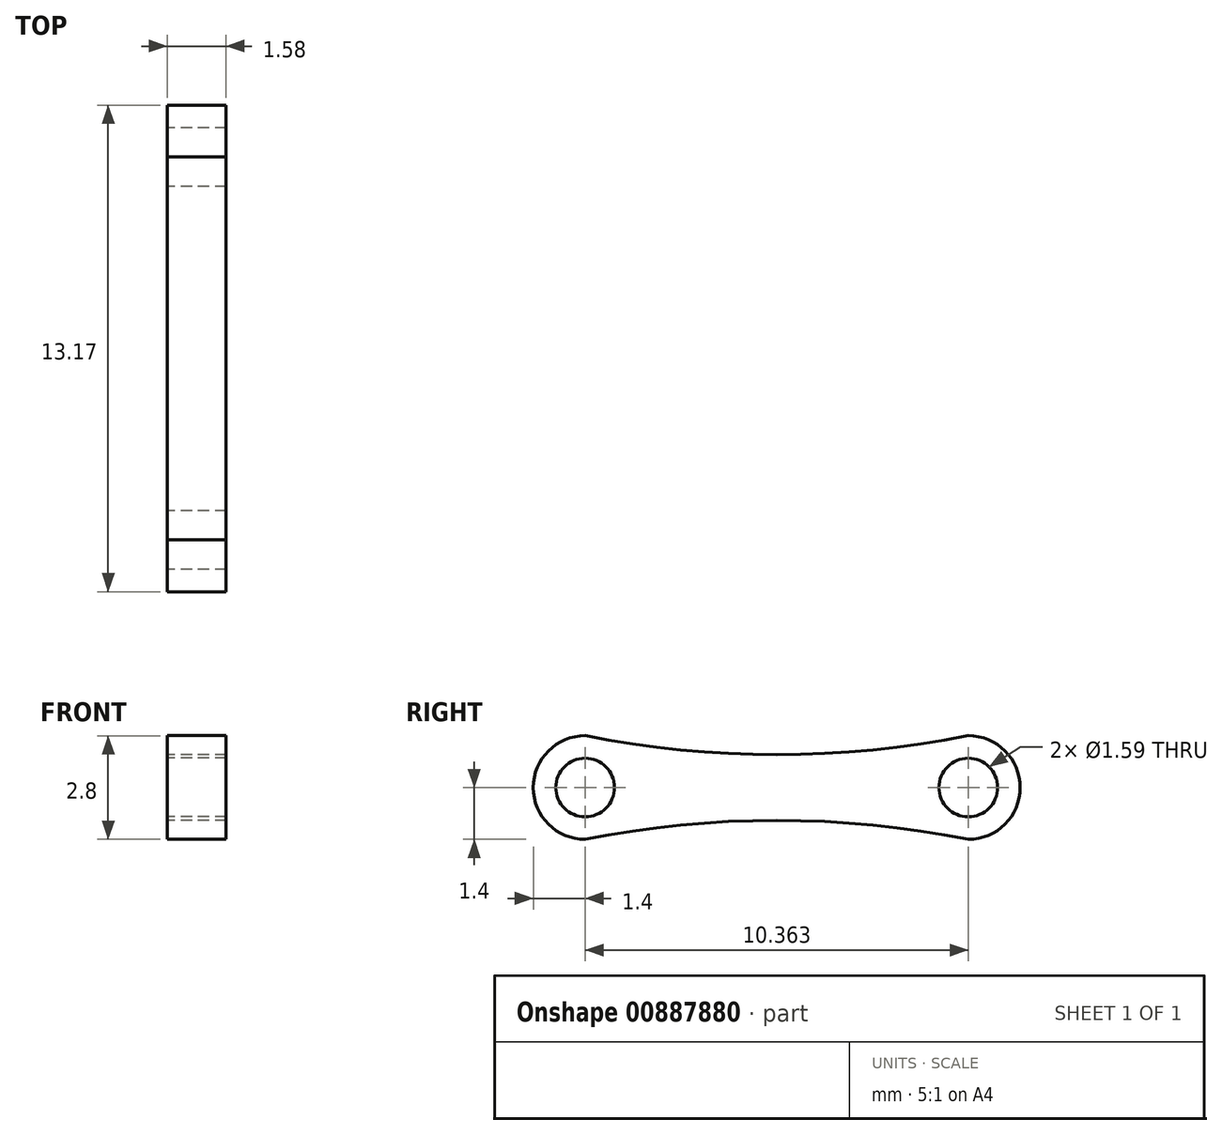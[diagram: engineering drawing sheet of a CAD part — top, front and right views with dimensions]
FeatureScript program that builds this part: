
annotation { "Feature Type Name" : "Feature", "Feature Type Description" : "" }
export const myFeature = defineFeature(function(context is Context, id is Id, definition is map)
    precondition{}
    {
        {
            var Q0;
            Q0=qCreatedBy(makeId("Right.planeOp"),FACE);
            var sketch = newSketch(context, id + "F0", { "sketchPlane" : qUnion([Q0])});
            skCircle(sketch, "E0", {"center": v(0, 0) * mm, "radius": 0.8 * mm});
            skCircle(sketch, "E1", {"center": v(10.36, 0) * mm, "radius": 0.8 * mm});
            skArc(sketch, "E2", {"start": v(1.23, -0.68) * mm, "mid": v(-1.4, 0) * mm, "end": v(1.23, 0.68) * mm});
            skArc(sketch, "E3", {"start": v(9.13, 0.68) * mm, "mid": v(11.77, 0) * mm, "end": v(9.13, -0.68) * mm});
            skArc(sketch, "E4", {"start": v(1.23, 0.68) * mm, "mid": v(5.18, 0.38) * mm, "end": v(9.13, 0.68) * mm});
            skArc(sketch, "E5", {"start": v(9.13, -0.68) * mm, "mid": v(5.18, -0.38) * mm, "end": v(1.23, -0.68) * mm});
            skArc(sketch, "E6", {"start": v(0, 1.4) * mm, "mid": v(5.18, 0.89) * mm, "end": v(10.36, 1.4) * mm});
            skArc(sketch, "E7", {"start": v(10.36, -1.4) * mm, "mid": v(5.18, -0.89) * mm, "end": v(0, -1.4) * mm});
            skSolve(sketch);
        }
        {
            var Q0;
            Q0=makeQuery(id+"F0.imprint","IMPRINT",FACE,{"disambiguationData":[TD([[makeQuery(id+"F0.imprint","IMPRINT",EDGE,{"derivedFrom":sQuery(id+"F0.wireOp",EDGE,"E0")}),-1.0]])]});
            extrude(context, id + "F1", {"entities" : qUnion([Q0]), "depth" : 1.59 * mm, "offsetDistance" : 25.4 * mm, "symmetric" : true});
        }
        {
            var Q0;
            {var subQ0=sQuery(id+"F0.wireOp",EDGE,"E4");Q0=makeQuery(id+"F0.imprint","IMPRINT",FACE,{"disambiguationData":[TD([[makeQuery(id+"F0.imprint","IMPRINT",EDGE,{"derivedFrom":subQ0}),1.0]])]});}
            var Q1;
            {var subQ0=sQuery(id+"F0.wireOp",EDGE,"E5");Q1=makeQuery(id+"F0.imprint","IMPRINT",FACE,{"disambiguationData":[TD([[makeQuery(id+"F0.imprint","IMPRINT",EDGE,{"derivedFrom":subQ0}),1.0]])]});}
            extrude(context, id + "F2", {"entities" : qUnion([Q0, Q1]), "operationType" : NewBodyOperationType.ADD, "depth" : 1.59 * mm, "offsetDistance" : 25.4 * mm, "symmetric" : true});
        }
    });
